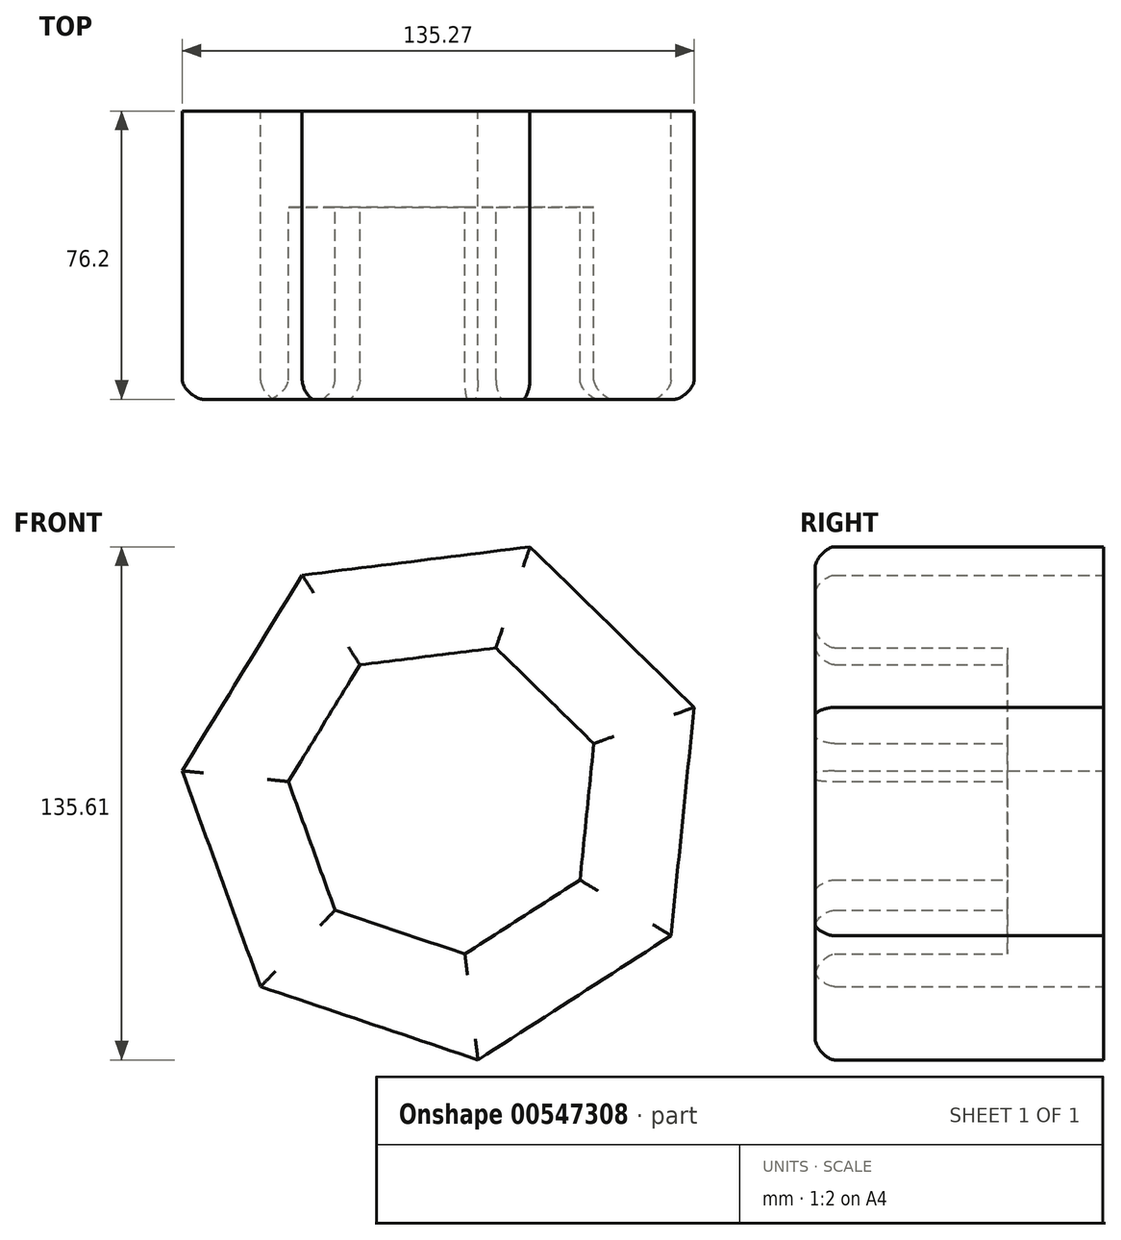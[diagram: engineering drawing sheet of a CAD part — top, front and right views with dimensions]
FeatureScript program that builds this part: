
annotation { "Feature Type Name" : "Feature", "Feature Type Description" : "" }
export const myFeature = defineFeature(function(context is Context, id is Id, definition is map)
    precondition{}
    {
        {
            var Q0;
            Q0=qCreatedBy(makeId("Front.planeOp"),FACE);
            var sketch = newSketch(context, id + "F0", { "sketchPlane" : qUnion([Q0])});
            skCircle(sketch, "E0.cCircle", {"center": v(0, 52.95) * mm, "radius": 62.98 * mm, "construction": true});
            skLineSegment(sketch, "E0.0", {"start": v(59.6, 16.43) * mm, "end": v(8.61, -16.43) * mm});
            skLineSegment(sketch, "E0.1", {"start": v(8.61, -16.43) * mm, "end": v(-48.87, 2.96) * mm});
            skLineSegment(sketch, "E0.2", {"start": v(-48.87, 2.96) * mm, "end": v(-69.55, 59.99) * mm});
            skLineSegment(sketch, "E0.3", {"start": v(-69.55, 59.99) * mm, "end": v(-37.86, 111.7) * mm});
            skLineSegment(sketch, "E0.4", {"start": v(-37.86, 111.7) * mm, "end": v(22.34, 119.18) * mm});
            skLineSegment(sketch, "E0.5", {"start": v(22.34, 119.18) * mm, "end": v(65.72, 76.78) * mm});
            skLineSegment(sketch, "E0.6", {"start": v(65.72, 76.78) * mm, "end": v(59.6, 16.43) * mm});
            skPoint(sketch, "E0.0.midPoint", {"position": v(34.1, 0) * mm});
            skSolve(sketch);
        }
        {
            var Q0;
            Q0=makeQuery(id+"F0.imprint","IMPRINT",FACE,{"disambiguationData":[TD([[makeQuery(id+"F0.imprint","IMPRINT",EDGE,{"derivedFrom":sQuery(id+"F0.wireOp",EDGE,"E0.0")}),-1.0]])]});
            extrude(context, id + "F1", {"entities" : qUnion([Q0]), "endBound" : BoundingType.SYMMETRIC, "depth" : 76.2 * mm, "offsetDistance" : 25.4 * mm});
        }
        {
            var Q0;
            Q0=makeQuery(id+"F1.opExtrude","CAP_FACE",FACE,{"disambiguationData":[OSD([sQuery(id+"F0.wireOp",EDGE,"E0.0"),sQuery(id+"F0.wireOp",EDGE,"E0.1"),sQuery(id+"F0.wireOp",EDGE,"E0.2"),sQuery(id+"F0.wireOp",EDGE,"E0.3"),sQuery(id+"F0.wireOp",EDGE,"E0.4"),sQuery(id+"F0.wireOp",EDGE,"E0.5"),sQuery(id+"F0.wireOp",EDGE,"E0.6")])],"isStart":false});
            shell(context, id + "F2", {"entities" : qUnion([Q0]), "thickness" : 25.4 * mm});
        }
        {
            var Q0;
            Q0=makeQuery(id+"F1.opExtrude","CAP_EDGE",EDGE,{"disambiguationData":[OSD([sQuery(id+"F0.wireOp",EDGE,"E0.5")])],"isStart":false});
            var Q1;
            Q1=makeQuery(id+"F1.opExtrude","CAP_EDGE",EDGE,{"disambiguationData":[OSD([sQuery(id+"F0.wireOp",EDGE,"E0.4")])],"isStart":false});
            var Q2;
            Q2=makeQuery(id+"F1.opExtrude","CAP_EDGE",EDGE,{"disambiguationData":[OSD([sQuery(id+"F0.wireOp",EDGE,"E0.3")])],"isStart":false});
            var Q3;
            Q3=makeQuery(id+"F1.opExtrude","CAP_EDGE",EDGE,{"disambiguationData":[OSD([sQuery(id+"F0.wireOp",EDGE,"E0.2")])],"isStart":false});
            var Q4;
            Q4=makeQuery(id+"F1.opExtrude","CAP_FACE",FACE,{"disambiguationData":[OSD([sQuery(id+"F0.wireOp",EDGE,"E0.0"),sQuery(id+"F0.wireOp",EDGE,"E0.1"),sQuery(id+"F0.wireOp",EDGE,"E0.2"),sQuery(id+"F0.wireOp",EDGE,"E0.3"),sQuery(id+"F0.wireOp",EDGE,"E0.4"),sQuery(id+"F0.wireOp",EDGE,"E0.5"),sQuery(id+"F0.wireOp",EDGE,"E0.6")])],"isStart":false});
            fillet(context, id + "F3", {"entities" : qUnion([Q0, Q1, Q2, Q3, Q4]), "radius" : 5.08 * mm, "tangentPropagation" : true, "rho" : 0.3, "crossSection" : FilletCrossSection.CONIC, "allowEdgeOverflow" : false});
        }
    });
